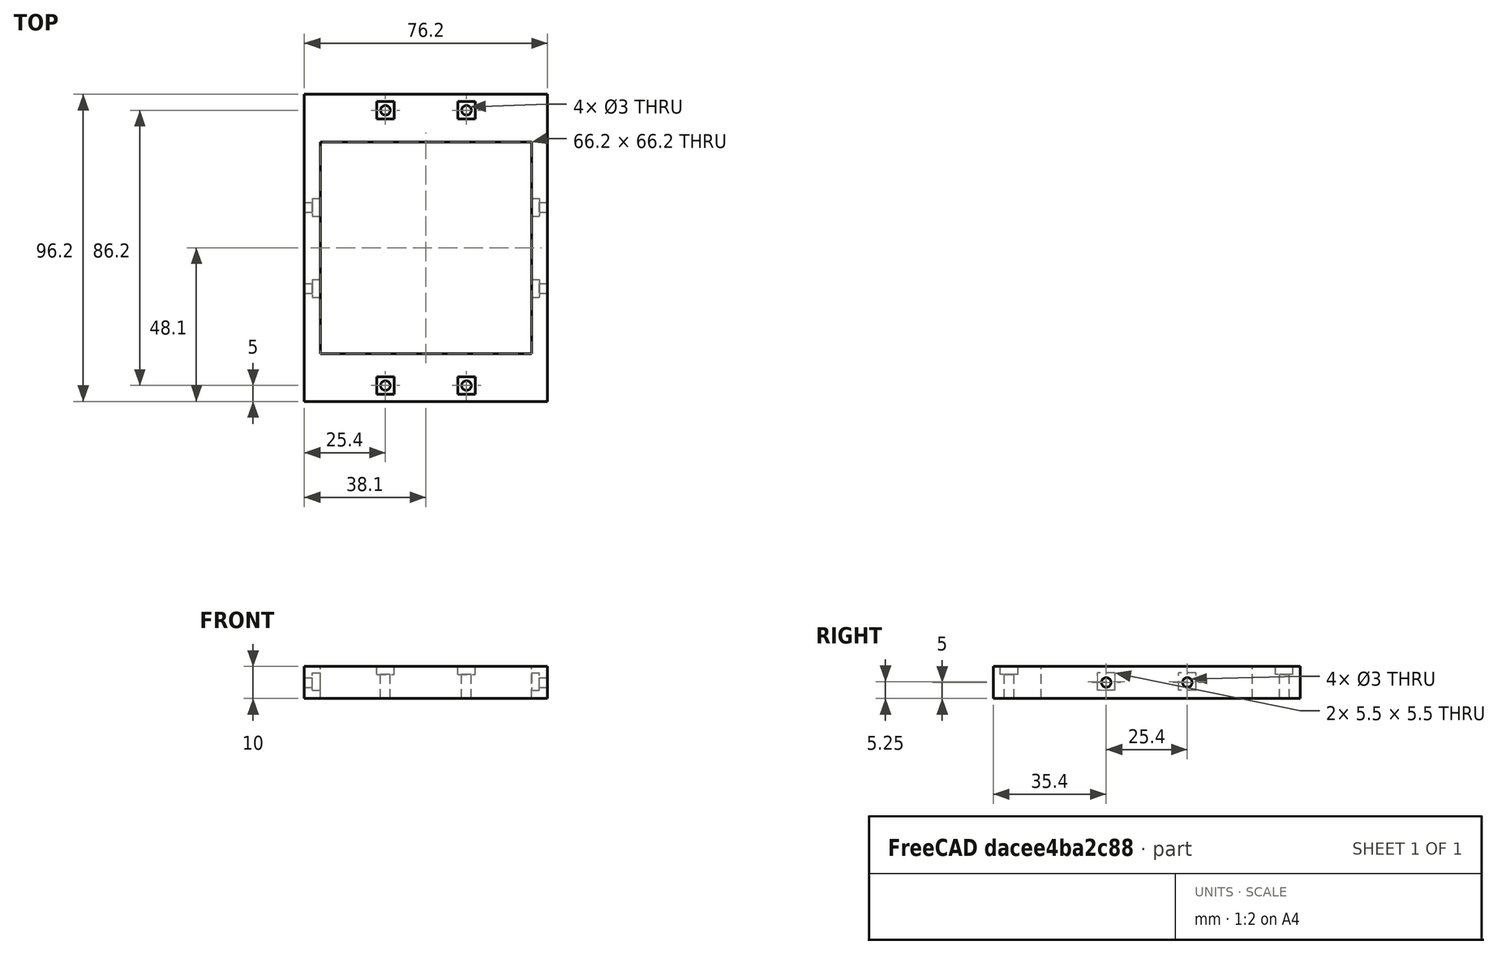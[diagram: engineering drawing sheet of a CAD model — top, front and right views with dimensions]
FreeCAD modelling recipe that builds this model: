
FCSTD DOCUMENT
Label: thickside
objects: Part::Cut×17, Part::Box×10, Part::Cylinder×8
note: 35 computed .brp shape members not serialized (recipe doc carries the construction recipe); baked Part::Feature solids carry a one-line shape summary decoded from their .brp

FEATURE [Part::Box] Box
  Height = 10
  Length = 76.2
  Width = 96.2
FEATURE [Part::Box] Box001
  Height = 10
  Length = 66.2
  Placement = pos=(5,15,0) rot=(0,0,1;0rad)
  Width = 66.2
FEATURE [Part::Cut] Cut
  Base = -> Box
  Tool = -> Box001
FEATURE [Part::Box] Box002
  Height = 5.5
  Length = 5.5
  Placement = pos=(71.19,38.15,2.5) rot=(0,0,-1;1.5708rad)
  Width = 2.5
FEATURE [Part::Box] Box003
  Height = 5.5
  Length = 5.5
  Placement = pos=(71.19,63.55,2.5) rot=(0,0,-1;1.5708rad)
  Width = 2.5
FEATURE [Part::Box] Box004
  Height = 5.5
  Length = 5.5
  Placement = pos=(2.5,63.55,2.5) rot=(0,0,-1;1.5708rad)
  Width = 2.5
FEATURE [Part::Box] Box005
  Height = 5.5
  Length = 5.5
  Placement = pos=(2.5,38.15,2.5) rot=(0,0,-1;1.5708rad)
  Width = 2.5
FEATURE [Part::Box] Box006
  Height = 5.5
  Length = 5.5
  Placement = pos=(22.65,7.75,7.5) rot=(1,0,0;1.5708rad)
  Width = 2.5
FEATURE [Part::Box] Box007
  Height = 5.5
  Length = 5.5
  Placement = pos=(48.05,7.75,7.5) rot=(1,0,0;1.5708rad)
  Width = 2.5
FEATURE [Part::Box] Box006001
  Height = 5.5
  Length = 5.5
  Placement = pos=(22.65,93.95,7.5) rot=(1,0,0;1.5708rad)
  Width = 2.5
FEATURE [Part::Box] Box007001
  Height = 5.5
  Length = 5.5
  Placement = pos=(48.05,93.95,7.5) rot=(1,0,0;1.5708rad)
  Width = 2.5
FEATURE [Part::Cut] Cut001
  Base = -> Cut
  Tool = -> Box002
FEATURE [Part::Cut] Cut002
  Base = -> Cut001
  Tool = -> Box007001
FEATURE [Part::Cut] Cut003
  Base = -> Cut002
  Tool = -> Box006001
FEATURE [Part::Cut] Cut004
  Base = -> Cut003
  Tool = -> Box007
FEATURE [Part::Cut] Cut005
  Base = -> Cut004
  Tool = -> Box006
FEATURE [Part::Cut] Cut006
  Base = -> Cut005
  Tool = -> Box005
FEATURE [Part::Cut] Cut007
  Base = -> Cut006
  Tool = -> Box004
FEATURE [Part::Cut] Cut008
  Base = -> Cut007
  Tool = -> Box003
FEATURE [Part::Cylinder] Cylinder002
  Angle = 360
  Height = 5
  Placement = pos=(71.2,60.8,5) rot=(0,1,0;1.5708rad)
  Radius = 1.5
FEATURE [Part::Cylinder] Cylinder002001
  Angle = 360
  Height = 5
  Placement = pos=(71.2,35.4,5) rot=(0,1,0;1.5708rad)
  Radius = 1.5
FEATURE [Part::Cylinder] Cylinder002002
  Angle = 360
  Height = 5
  Placement = pos=(-0.8,60.8,5) rot=(0,1,0;1.5708rad)
  Radius = 1.5
FEATURE [Part::Cylinder] Cylinder002001001
  Angle = 360
  Height = 5
  Placement = pos=(-0.8,35.4,5) rot=(0,1,0;1.5708rad)
  Radius = 1.5
FEATURE [Part::Cylinder] Cylinder
  Angle = 360
  Height = 10
  Placement = pos=(25.4,5,0) rot=(0,0,1;0rad)
  Radius = 1.5
FEATURE [Part::Cylinder] Cylinder002001002
  Angle = 360
  Height = 10
  Placement = pos=(50.8,5,0) rot=(0,0,1;0rad)
  Radius = 1.5
FEATURE [Part::Cylinder] Cylinder002001003
  Angle = 360
  Height = 10
  Placement = pos=(25.4,91.2,0) rot=(0,0,1;0rad)
  Radius = 1.5
FEATURE [Part::Cylinder] Cylinder002001002001
  Angle = 360
  Height = 10
  Placement = pos=(50.8,91.2,0) rot=(0,0,1;0rad)
  Radius = 1.5
FEATURE [Part::Cut] Cut009
  Base = -> Cut008
  Tool = -> Cylinder002
FEATURE [Part::Cut] Cut010
  Base = -> Cut009
  Tool = -> Cylinder002001002001
FEATURE [Part::Cut] Cut011
  Base = -> Cut010
  Tool = -> Cylinder002001003
FEATURE [Part::Cut] Cut012
  Base = -> Cut011
  Tool = -> Cylinder002001002
FEATURE [Part::Cut] Cut013
  Base = -> Cut012
  Tool = -> Cylinder
FEATURE [Part::Cut] Cut014
  Base = -> Cut013
  Tool = -> Cylinder002001001
FEATURE [Part::Cut] Cut015
  Base = -> Cut014
  Tool = -> Cylinder002002
FEATURE [Part::Cut] Cut016
  Base = -> Cut015
  Tool = -> Cylinder002001
